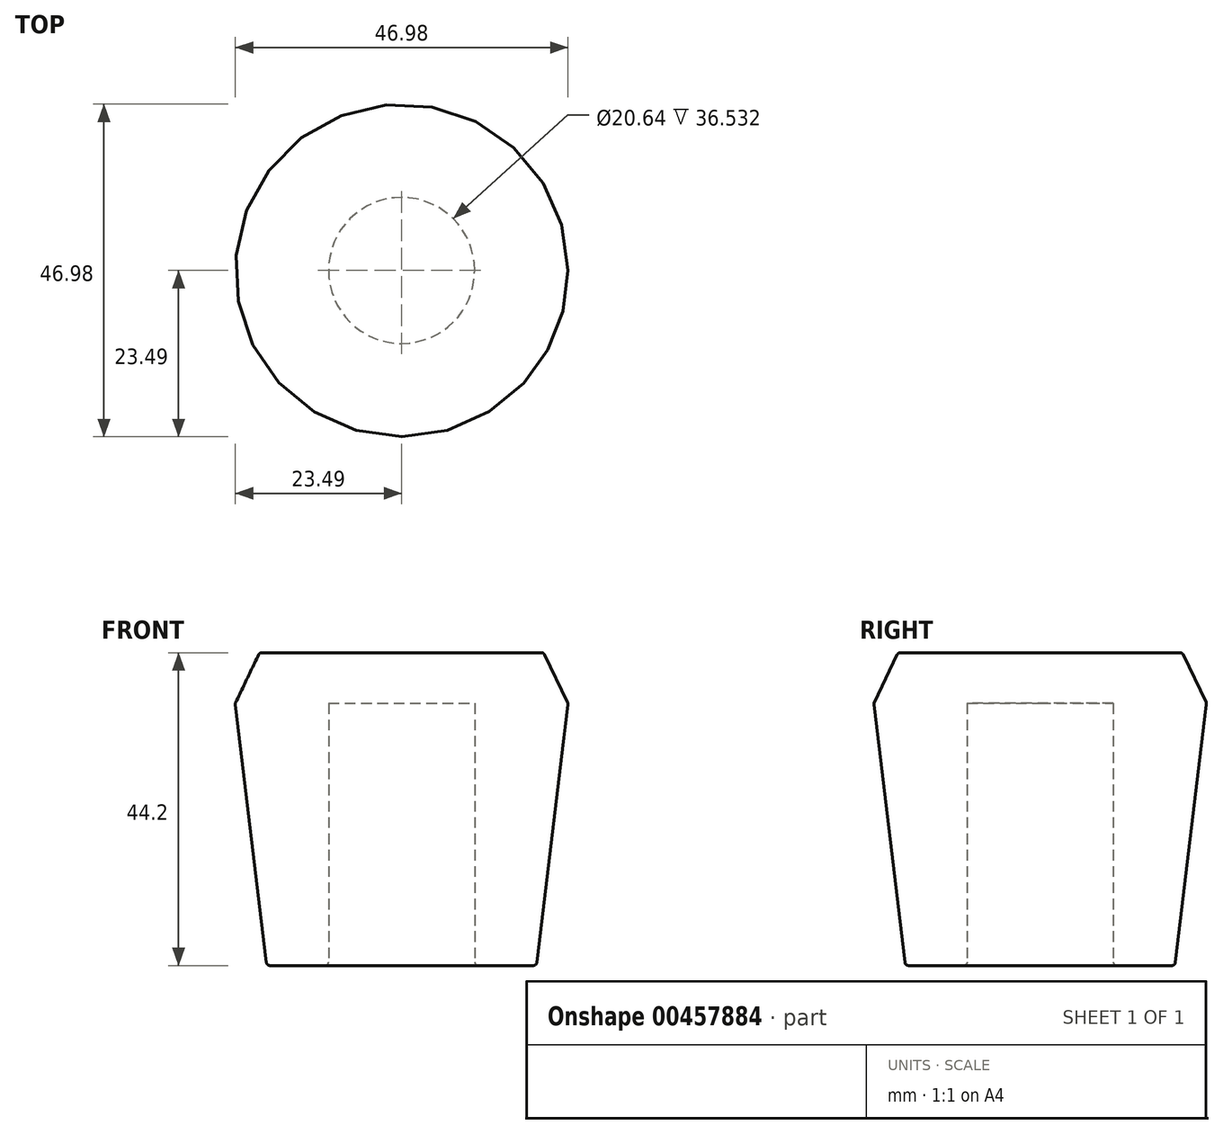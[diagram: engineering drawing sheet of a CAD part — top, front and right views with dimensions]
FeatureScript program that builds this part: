
annotation { "Feature Type Name" : "Feature", "Feature Type Description" : "" }
export const myFeature = defineFeature(function(context is Context, id is Id, definition is map)
    precondition{}
    {
        {
            var Q0;
            Q0=qCreatedBy(makeId("Front.planeOp"),FACE);
            var sketch = newSketch(context, id + "F0", { "sketchPlane" : qUnion([Q0])});
            skLineSegment(sketch, "E0", {"start": v(0, 0) * mm, "end": v(10.32, 0) * mm, "construction": true});
            skLineSegment(sketch, "E1", {"start": v(10.32, 0) * mm, "end": v(19.05, 0) * mm});
            skLineSegment(sketch, "E2", {"start": v(0, 0) * mm, "end": v(0, 44.2) * mm, "construction": true});
            skLineSegment(sketch, "E3", {"start": v(0, 44.2) * mm, "end": v(20.07, 44.2) * mm});
            skLineSegment(sketch, "E4", {"start": v(20.07, 44.2) * mm, "end": v(23.5, 37.04) * mm});
            skLineSegment(sketch, "E5", {"start": v(19.05, 0) * mm, "end": v(23.5, 37.04) * mm});
            skLineSegment(sketch, "E6", {"start": v(10.32, 0) * mm, "end": v(10.32, 37.04) * mm});
            skLineSegment(sketch, "E7", {"start": v(10.32, 37.04) * mm, "end": v(0, 37.04) * mm});
            skLineSegment(sketch, "E8", {"start": v(0, 37.04) * mm, "end": v(0, 44.2) * mm});
            skSolve(sketch);
        }
        {
            var Q0;
            Q0=makeQuery(id+"F0.imprint","IMPRINT",FACE,{"disambiguationData":[TD([[makeQuery(id+"F0.imprint","IMPRINT",EDGE,{"derivedFrom":sQuery(id+"F0.wireOp",EDGE,"E1")}),1.0]])]});
            var Q1;
            Q1=sQuery(id+"F0.wireOp",EDGE,"E2");
            revolve(context, id + "F1", {"entities" : qUnion([Q0]), "axis" : qUnion([Q1]), "revolveType" : RevolveType.FULL});
        }
        {
            var Q0;
            Q0=makeQuery(id+"F1.opRevolve","SWEPT_EDGE",EDGE,{"disambiguationData":[OSD([sQuery(id+"F0.wireOp",EDGE,"E3"),sQuery(id+"F0.wireOp",EDGE,"E4")])]});
            var Q1;
            Q1=makeQuery(id+"F1.opRevolve","SWEPT_EDGE",EDGE,{"disambiguationData":[OSD([sQuery(id+"F0.wireOp",EDGE,"E1"),sQuery(id+"F0.wireOp",EDGE,"E5")])]});
            var Q2;
            Q2=makeQuery(id+"F1.opRevolve","SWEPT_EDGE",EDGE,{"disambiguationData":[OSD([sQuery(id+"F0.wireOp",EDGE,"E4"),sQuery(id+"F0.wireOp",EDGE,"E5")])]});
            var Q3;
            Q3=makeQuery(id+"F1.opRevolve","SWEPT_EDGE",EDGE,{"disambiguationData":[OSD([sQuery(id+"F0.wireOp",EDGE,"E1"),sQuery(id+"F0.wireOp",EDGE,"E6")])]});
            fillet(context, id + "F2", {"entities" : qUnion([Q0, Q1, Q2, Q3]), "radius" : 0.5 * mm, "tangentPropagation" : true, "allowEdgeOverflow" : false});
        }
    });
